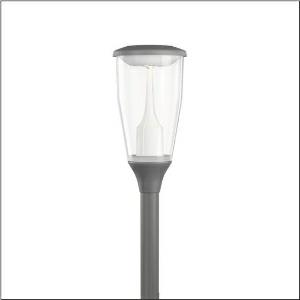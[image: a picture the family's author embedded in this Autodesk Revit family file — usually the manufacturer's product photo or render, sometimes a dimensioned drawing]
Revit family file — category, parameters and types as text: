
# Revit family: dl_11_iq___st1_2a_5xa5575af14h000022_aeb9
name_source: partatom
category: Lighting Fixtures
units: mm (PartAtom-declared; Revit-internal decimal feet)

## family parameters
Cut with Voids When Loaded = No
Host = Face
Light Source = No
Part Type = Normal
Room Calculation Point = No
Round Connector Dimension = Use Diameter
Shared = No

## types (1)
- --- (1 x LED, 1560 lm, 12.9 W, 2200K)
    Apparent Load = 13 VA
    CIE Flux Codes = 24 63 94 96 100
    Color Rendering = 70
    Color Temperature = 2200K
    Default Elevation = 1800 mm
    Description = DL 11 iQ, mast luminaire, Module 540 iQ-SR, primary light control with 3 zone facetted reflector, of plastic, silver coated, highly specular, structured, primary optical cover: cover, of PMMA, transparent, light distribution: ST1.2a, light emission: direct distribution, primary light characteristic: asymmetric, installation type: post-top, LED, High Power LED, rated luminous flux: 1.560lm, luminous efficacy: 149lm/W, light colour: 722, colour temperature: 2200K, control gear: iQ Street-Remote, control: Street-Remote, Auto-Match, Temp-Guard, Lumen-Switch, Night-Set, Smart-Wire, Light-Fading, Desk-Remote (wireless, voltage-free reading and setting of iQ features in the workshop via application-optimized NFC function/RFID function), optimised constant luminous flux control (CLO 2.0), mains connection: 220..240V, AC, 50/60Hz, connection cable pre-assembled, cable length: 5,5m, wiring characteristics: H07RN-F, 5-core, 1.5mm², start of lifetime: 13W, end of service life: 13W, reduction: 5W, luminaire housing, upper part, of diecast aluminium, coated, SITECO metallic grey (DB 702S), spigot size: 76mm (post-top), mounting height: 3..5m, post-top mast mounting element, of diecast aluminium, coated, SITECO metallic grey (DB 702S), Module 540 iQ-SR, traffic white (RAL 9016), equipment: standard, protection rating (complete): IP66, insulation class (complete): insulation class II (safety insulation), certification: CE, ENEC, ENEC+, VDE, impact resistance: IK07, packaging unit: 1 piece

Light Distribution: ST1.2a
    Height = 665 mm
    Lamp = 1 x LED
    Lamp Light Flux = 1560 lm
    Lamp Power = 12.9 W
    Lamp count = 1
    Length = 334 mm
    Luminous efficacy = 121 lm/W
    Manufacturer = Siteco
    ModVariant = No
    Model = 5XA5575AF14H000022
    Number of Poles = 1
    OnlyDefault = Yes
    Power Factor = 1
    Product Name = DL 11 iQ | ST1.2a
    Product group = mast luminaire | pylon top
    ProductGroupID = 6100
    Protection Class = Protection class II
    Protection Degree = IP 66
    RLX_Detail_Level = 1
    RLX_Emergency_Light_Flux = 0 lm
    RLX_Emergency_Type = 0
    RLX_Emergency_Type_DB = No
    RlxData = <blob elided: 152813 chars, md5=d77e50bd>
    Socket = socket
    Standby Power = 0 W
    System Light Flux = 1560 lm
    System Power = 13 W
    Type Comments = factory setting: luminous flux: 100 % | dim-lin: 254 | 516 mA
    Type Image = l_1258354.jpg
    URL = http://relux.com
    VarID = @adj_098855
    Voltage = 0 V
    Weight = 0.00 kg
    Width = 0 mm  [stored 0 ft]

note: [stored X ft] marks values corroborated as IEEE doubles in the binary element streams (Revit-internal decimal feet)

## geometry (parser evidence)
native form markers: Blend x4, Sweep x9
no freeform markers — native parametric forms only
